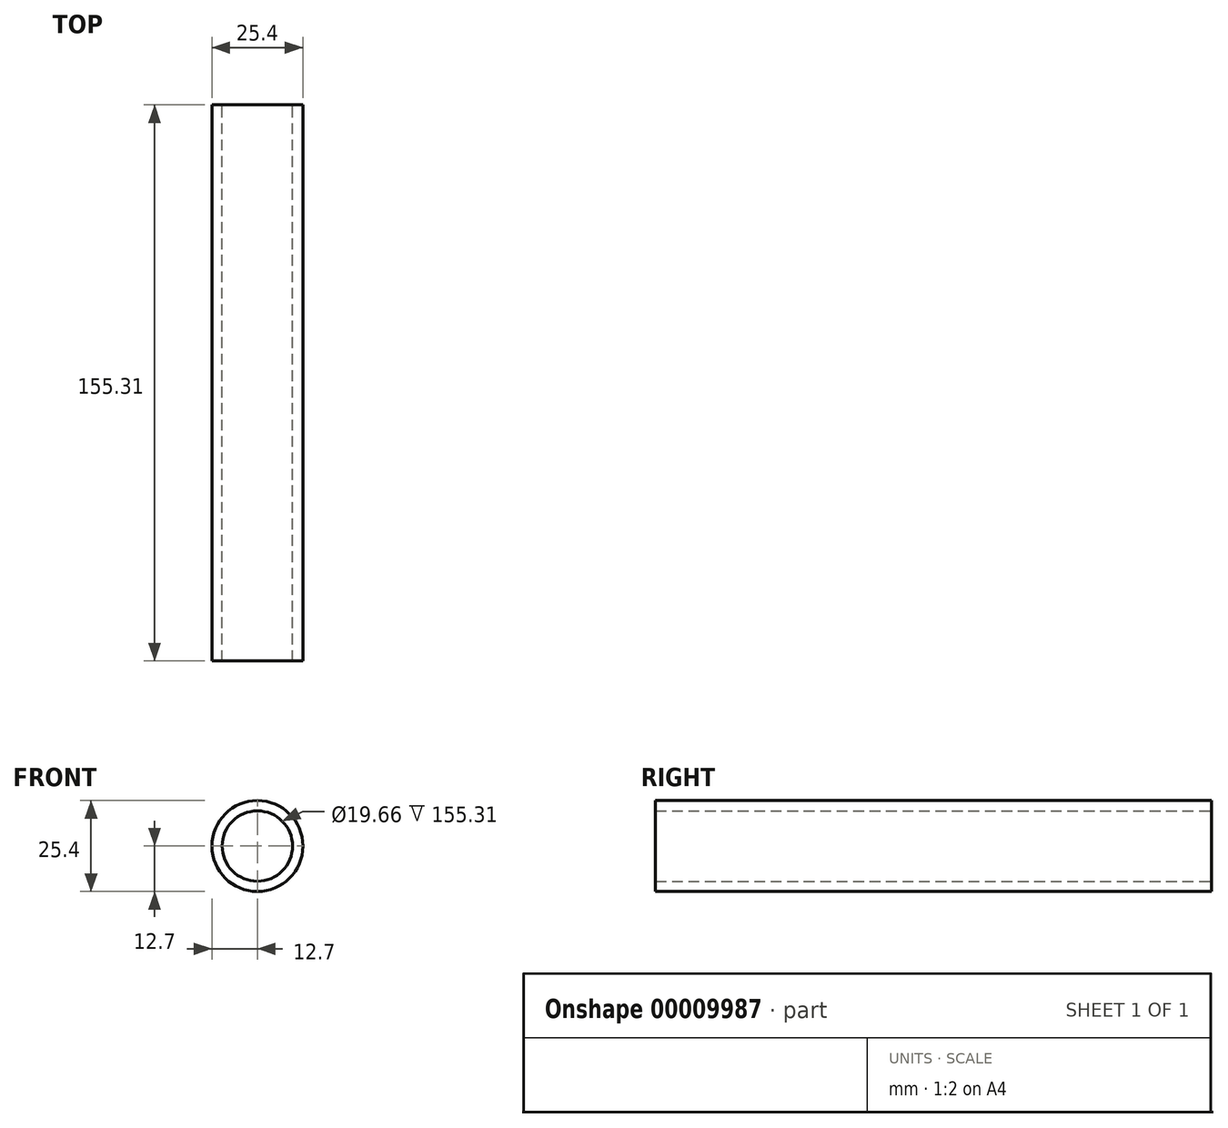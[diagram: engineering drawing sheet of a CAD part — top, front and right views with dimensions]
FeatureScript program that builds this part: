
annotation { "Feature Type Name" : "Feature", "Feature Type Description" : "" }
export const myFeature = defineFeature(function(context is Context, id is Id, definition is map)
    precondition{}
    {
        {
            var Q0;
            Q0=qCreatedBy(makeId("Front.planeOp"),FACE);
            var sketch = newSketch(context, id + "F0", { "sketchPlane" : qUnion([Q0])});
            skCircle(sketch, "E0", {"center": v(0, 0) * mm, "radius": 12.7 * mm});
            skCircle(sketch, "E1", {"center": v(0, 0) * mm, "radius": 9.83 * mm});
            skSolve(sketch);
        }
        {
            var Q0;
            Q0=qSketchRegion(id+"F0",true);
            extrude(context, id + "F1", {"entities" : qUnion([Q0]), "depth" : 304.8 * mm - 201.23 * mm + 51.74 * mm});
        }
    });
